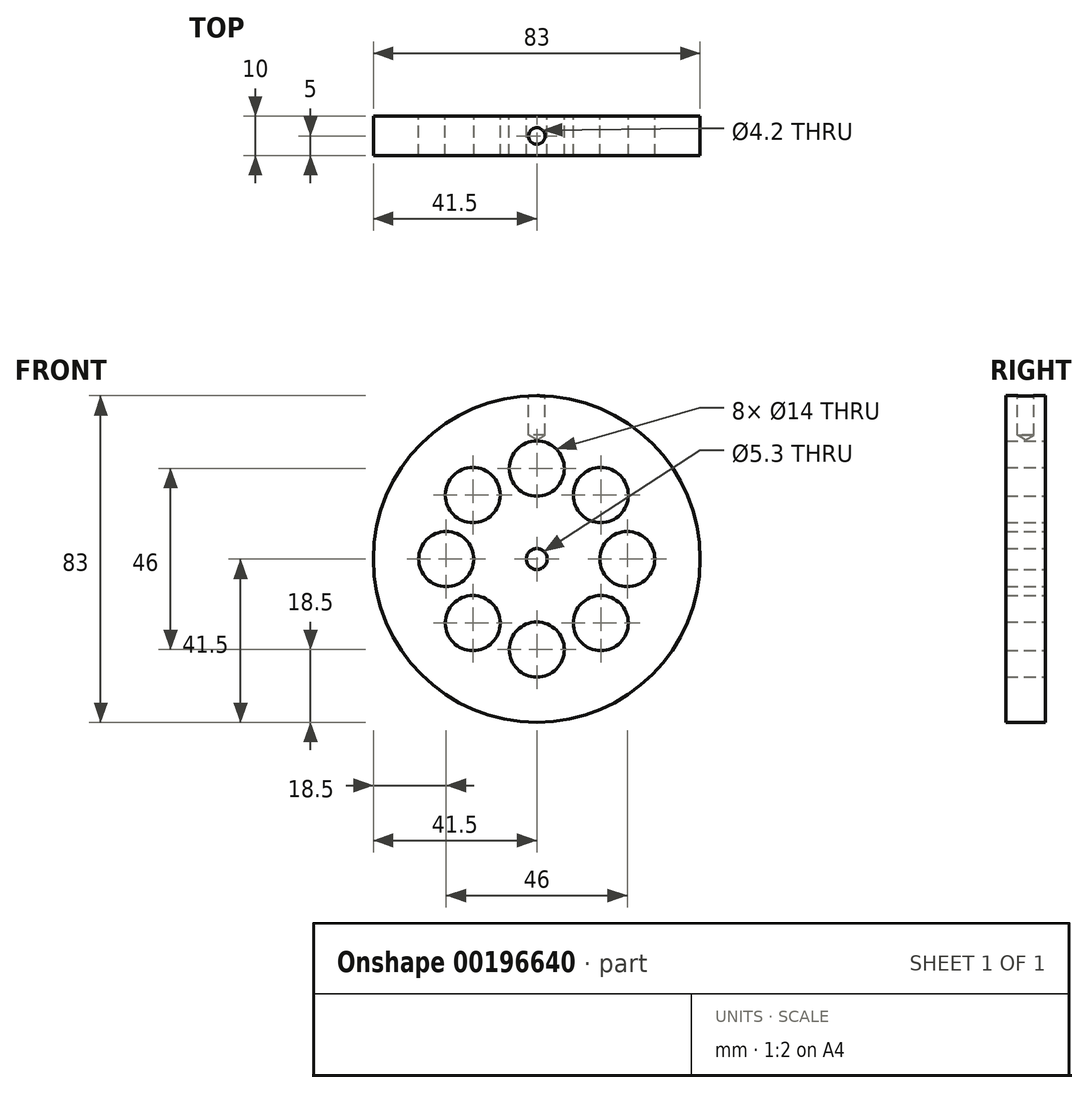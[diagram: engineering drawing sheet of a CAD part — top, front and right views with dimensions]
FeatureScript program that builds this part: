
annotation { "Feature Type Name" : "Feature", "Feature Type Description" : "" }
export const myFeature = defineFeature(function(context is Context, id is Id, definition is map)
    precondition{}
    {
        {
            var Q0;
            Q0=qCreatedBy(makeId("Front.planeOp"),FACE);
            var sketch = newSketch(context, id + "F0", { "sketchPlane" : qUnion([Q0])});
            skCircle(sketch, "E0", {"center": v(0, 0) * mm, "radius": 41.5 * mm});
            skCircle(sketch, "E1", {"center": v(0, 0) * mm, "radius": 2.65 * mm});
            skCircle(sketch, "E2", {"center": v(0, 23) * mm, "radius": 7 * mm});
            skCircle(sketch, "E3.1.0", {"center": v(-16.26, 16.26) * mm, "radius": 7 * mm});
            skCircle(sketch, "E3.2.0", {"center": v(-23, 0) * mm, "radius": 7 * mm});
            skCircle(sketch, "E3.3.0", {"center": v(-16.26, -16.26) * mm, "radius": 7 * mm});
            skCircle(sketch, "E3.4.0", {"center": v(0, -23) * mm, "radius": 7 * mm});
            skCircle(sketch, "E3.5.0", {"center": v(16.26, -16.26) * mm, "radius": 7 * mm});
            skCircle(sketch, "E3.6.0", {"center": v(23, 0) * mm, "radius": 7 * mm});
            skCircle(sketch, "E3.7.0", {"center": v(16.26, 16.26) * mm, "radius": 7 * mm});
            skSolve(sketch);
        }
        {
            var Q0;
            Q0=makeQuery(id+"F0.imprint","IMPRINT",FACE,{"disambiguationData":[TD([[makeQuery(id+"F0.imprint","IMPRINT",EDGE,{"derivedFrom":sQuery(id+"F0.wireOp",EDGE,"E0")}),1.0]])]});
            extrude(context, id + "F1", {"entities" : qUnion([Q0]), "endBound" : BoundingType.SYMMETRIC, "depth" : 10 * mm});
        }
        {
            var Q0;
            Q0=qCreatedBy(makeId("Top.planeOp"),FACE);
            cPlane(context, id + "F2", {"entities" : qUnion([Q0]), "cplaneType" : CPlaneType.OFFSET, "offset" : 41.5 * mm, "width" : 150 * mm, "height" : 150 * mm});
        }
        {
            var Q0;
            Q0=qCreatedBy(id+"F2.planeOp",FACE);
            var sketch = newSketch(context, id + "F3", { "sketchPlane" : qUnion([Q0])});
            skPoint(sketch, "E4", {"position": v(0, 0) * mm});
            skSolve(sketch);
        }
        {
            var Q0;
            Q0=sQuery(id+"F3.wireOp",VERTEX,"E4");
            var Q1;
            Q1=makeQuery(id+"F1.opExtrude","SWEPT_BODY",BODY,{"disambiguationData":[OSD([sQuery(id+"F0.wireOp",EDGE,"E0"),sQuery(id+"F0.wireOp",EDGE,"E1"),sQuery(id+"F0.wireOp",EDGE,"E2"),sQuery(id+"F0.wireOp",EDGE,"E3.1.0"),sQuery(id+"F0.wireOp",EDGE,"E3.2.0"),sQuery(id+"F0.wireOp",EDGE,"E3.3.0"),sQuery(id+"F0.wireOp",EDGE,"E3.4.0"),sQuery(id+"F0.wireOp",EDGE,"E3.5.0"),sQuery(id+"F0.wireOp",EDGE,"E3.6.0"),sQuery(id+"F0.wireOp",EDGE,"E3.7.0")])]});
            hole(context, id + "F4", {"style" : HoleStyle.SIMPLE, "endStyle" : HoleEndStyle.BLIND, "standardTappedOrClearance" : lookupTablePath({ "standard" : "ISO", "engagement" : "75%", "pitch" : "0.8 mm", "size" : "M5", "type" : "Tapped" }), "standardBlindInLast" : lookupTablePath({ "standard" : "ISO", "engagement" : "75%", "pitch" : "0.8 mm", "size" : "M5", "type" : "Tapped" }), "holeDiameter" : 4.2 * mm, "holeDepth" : 10 * mm, "startFromSketch" : true, "locations" : qUnion([Q0]), "scope" : qUnion([Q1]), "majorDiameter" : 5 * mm});
        }
    });
